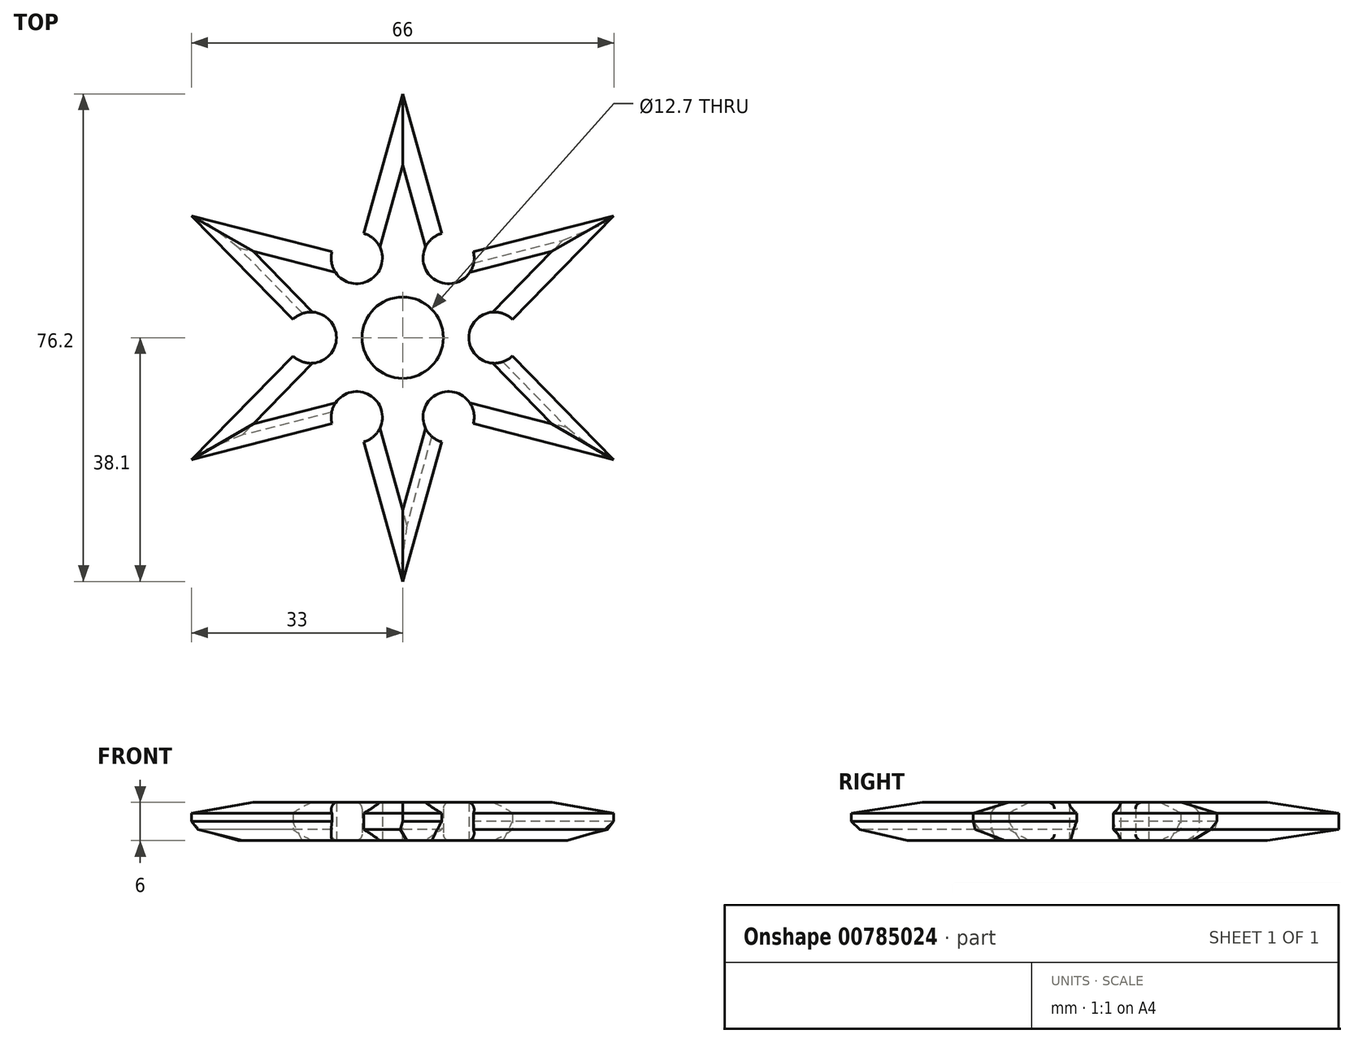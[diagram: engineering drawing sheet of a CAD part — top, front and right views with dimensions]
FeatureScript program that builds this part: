
annotation { "Feature Type Name" : "Feature", "Feature Type Description" : "" }
export const myFeature = defineFeature(function(context is Context, id is Id, definition is map)
    precondition{}
    {
        {
            var Q0;
            Q0=qCreatedBy(makeId("Top.planeOp"),FACE);
            var sketch = newSketch(context, id + "F0", { "sketchPlane" : qUnion([Q0])});
            skCircle(sketch, "E0", {"center": v(0, 0) * mm, "radius": 6.35 * mm});
            skLineSegment(sketch, "E1", {"start": v(0, 38.1) * mm, "end": v(-6.1, 16.28) * mm});
            skLineSegment(sketch, "E2.MirrorCS", {"start": v(0, 38.1) * mm, "end": v(6.1, 16.28) * mm});
            skLineSegment(sketch, "E3.1.0", {"start": v(-33, 19.05) * mm, "end": v(-11.05, 13.42) * mm});
            skLineSegment(sketch, "E3.1.1", {"start": v(-33, 19.05) * mm, "end": v(-17.15, 2.86) * mm});
            skLineSegment(sketch, "E3.2.0", {"start": v(-33, -19.05) * mm, "end": v(-17.15, -2.86) * mm});
            skLineSegment(sketch, "E3.2.1", {"start": v(-33, -19.05) * mm, "end": v(-11.05, -13.42) * mm});
            skLineSegment(sketch, "E3.3.0", {"start": v(0, -38.1) * mm, "end": v(-6.1, -16.28) * mm});
            skLineSegment(sketch, "E3.3.1", {"start": v(0, -38.1) * mm, "end": v(6.1, -16.28) * mm});
            skLineSegment(sketch, "E3.4.0", {"start": v(33, -19.05) * mm, "end": v(11.05, -13.42) * mm});
            skLineSegment(sketch, "E3.4.1", {"start": v(33, -19.05) * mm, "end": v(17.15, -2.86) * mm});
            skLineSegment(sketch, "E3.5.0", {"start": v(33, 19.05) * mm, "end": v(17.15, 2.86) * mm});
            skLineSegment(sketch, "E3.5.1", {"start": v(33, 19.05) * mm, "end": v(11.05, 13.42) * mm});
            skArc(sketch, "E4", {"start": v(-11.05, 13.42) * mm, "mid": v(-5.18, 8.96) * mm, "end": v(-6.1, 16.28) * mm});
            skArc(sketch, "E5.1.0", {"start": v(-17.15, -2.86) * mm, "mid": v(-10.35, 0) * mm, "end": v(-17.15, 2.86) * mm});
            skArc(sketch, "E5.2.0", {"start": v(-6.1, -16.28) * mm, "mid": v(-5.17, -8.96) * mm, "end": v(-11.05, -13.42) * mm});
            skArc(sketch, "E5.3.0", {"start": v(11.05, -13.42) * mm, "mid": v(5.18, -8.96) * mm, "end": v(6.1, -16.28) * mm});
            skArc(sketch, "E5.4.0", {"start": v(17.15, 2.86) * mm, "mid": v(10.35, 0) * mm, "end": v(17.15, -2.86) * mm});
            skArc(sketch, "E5.5.0", {"start": v(6.1, 16.28) * mm, "mid": v(5.17, 8.96) * mm, "end": v(11.05, 13.42) * mm});
            skPoint(sketch, "E6.orphan", {"position": v(7.18, 12.43) * mm});
            skSolve(sketch);
        }
        {
            var Q0;
            Q0=makeQuery(id+"F0.imprint","IMPRINT",FACE,{"disambiguationData":[TD([[makeQuery(id+"F0.imprint","IMPRINT",EDGE,{"derivedFrom":sQuery(id+"F0.wireOp",EDGE,"E0")}),-1.0]])]});
            extrude(context, id + "F1", {"entities" : qUnion([Q0]), "depth" : 6 * mm, "offsetDistance" : 25 * mm});
        }
        {
            var Q0;
            Q0=makeQuery(id+"F1.opExtrude","CAP_EDGE",EDGE,{"disambiguationData":[OSD([sQuery(id+"F0.wireOp",EDGE,"E1")])],"isStart":false});
            var Q1;
            Q1=makeQuery(id+"F1.opExtrude","CAP_EDGE",EDGE,{"disambiguationData":[OSD([sQuery(id+"F0.wireOp",EDGE,"E2.MirrorCS")])],"isStart":false});
            var Q2;
            Q2=makeQuery(id+"F1.opExtrude","CAP_EDGE",EDGE,{"disambiguationData":[OSD([sQuery(id+"F0.wireOp",EDGE,"E3.5.1")])],"isStart":false});
            var Q3;
            Q3=makeQuery(id+"F1.opExtrude","CAP_EDGE",EDGE,{"disambiguationData":[OSD([sQuery(id+"F0.wireOp",EDGE,"E3.5.0")])],"isStart":false});
            var Q4;
            Q4=makeQuery(id+"F1.opExtrude","CAP_EDGE",EDGE,{"disambiguationData":[OSD([sQuery(id+"F0.wireOp",EDGE,"E3.4.1")])],"isStart":false});
            var Q5;
            Q5=makeQuery(id+"F1.opExtrude","CAP_EDGE",EDGE,{"disambiguationData":[OSD([sQuery(id+"F0.wireOp",EDGE,"E3.4.0")])],"isStart":false});
            var Q6;
            Q6=makeQuery(id+"F1.opExtrude","CAP_EDGE",EDGE,{"disambiguationData":[OSD([sQuery(id+"F0.wireOp",EDGE,"E3.3.1")])],"isStart":false});
            var Q7;
            Q7=makeQuery(id+"F1.opExtrude","CAP_EDGE",EDGE,{"disambiguationData":[OSD([sQuery(id+"F0.wireOp",EDGE,"E3.3.0")])],"isStart":false});
            var Q8;
            Q8=makeQuery(id+"F1.opExtrude","CAP_EDGE",EDGE,{"disambiguationData":[OSD([sQuery(id+"F0.wireOp",EDGE,"E3.2.1")])],"isStart":false});
            var Q9;
            Q9=makeQuery(id+"F1.opExtrude","CAP_EDGE",EDGE,{"disambiguationData":[OSD([sQuery(id+"F0.wireOp",EDGE,"E3.2.0")])],"isStart":false});
            var Q10;
            Q10=makeQuery(id+"F1.opExtrude","CAP_EDGE",EDGE,{"disambiguationData":[OSD([sQuery(id+"F0.wireOp",EDGE,"E3.1.1")])],"isStart":false});
            var Q11;
            Q11=makeQuery(id+"F1.opExtrude","CAP_EDGE",EDGE,{"disambiguationData":[OSD([sQuery(id+"F0.wireOp",EDGE,"E3.1.0")])],"isStart":false});
            var Q12;
            Q12=makeQuery(id+"F1.opExtrude","CAP_EDGE",EDGE,{"disambiguationData":[OSD([sQuery(id+"F0.wireOp",EDGE,"E3.3.1")])],"isStart":true});
            var Q13;
            Q13=makeQuery(id+"F1.opExtrude","CAP_EDGE",EDGE,{"disambiguationData":[OSD([sQuery(id+"F0.wireOp",EDGE,"E3.3.0")])],"isStart":true});
            var Q14;
            Q14=makeQuery(id+"F1.opExtrude","CAP_EDGE",EDGE,{"disambiguationData":[OSD([sQuery(id+"F0.wireOp",EDGE,"E3.2.1")])],"isStart":true});
            var Q15;
            Q15=makeQuery(id+"F1.opExtrude","CAP_EDGE",EDGE,{"disambiguationData":[OSD([sQuery(id+"F0.wireOp",EDGE,"E3.2.0")])],"isStart":true});
            var Q16;
            Q16=makeQuery(id+"F1.opExtrude","CAP_EDGE",EDGE,{"disambiguationData":[OSD([sQuery(id+"F0.wireOp",EDGE,"E3.1.1")])],"isStart":true});
            var Q17;
            Q17=makeQuery(id+"F1.opExtrude","CAP_EDGE",EDGE,{"disambiguationData":[OSD([sQuery(id+"F0.wireOp",EDGE,"E3.1.0")])],"isStart":true});
            var Q18;
            Q18=makeQuery(id+"F1.opExtrude","CAP_EDGE",EDGE,{"disambiguationData":[OSD([sQuery(id+"F0.wireOp",EDGE,"E1")])],"isStart":true});
            var Q19;
            Q19=makeQuery(id+"F1.opExtrude","CAP_EDGE",EDGE,{"disambiguationData":[OSD([sQuery(id+"F0.wireOp",EDGE,"E2.MirrorCS")])],"isStart":true});
            var Q20;
            Q20=makeQuery(id+"F1.opExtrude","CAP_EDGE",EDGE,{"disambiguationData":[OSD([sQuery(id+"F0.wireOp",EDGE,"E3.5.1")])],"isStart":true});
            var Q21;
            Q21=makeQuery(id+"F1.opExtrude","CAP_EDGE",EDGE,{"disambiguationData":[OSD([sQuery(id+"F0.wireOp",EDGE,"E3.5.0")])],"isStart":true});
            var Q22;
            Q22=makeQuery(id+"F1.opExtrude","CAP_EDGE",EDGE,{"disambiguationData":[OSD([sQuery(id+"F0.wireOp",EDGE,"E3.4.1")])],"isStart":true});
            var Q23;
            Q23=makeQuery(id+"F1.opExtrude","CAP_EDGE",EDGE,{"disambiguationData":[OSD([sQuery(id+"F0.wireOp",EDGE,"E3.4.0")])],"isStart":true});
            chamfer(context, id + "F2", {"entities" : qUnion([Q0, Q1, Q2, Q3, Q4, Q5, Q6, Q7, Q8, Q9, Q10, Q11, Q12, Q13, Q14, Q15, Q16, Q17, Q18, Q19, Q20, Q21, Q22, Q23]), "chamferType" : ChamferType.OFFSET_ANGLE, "width" : 3 * mm, "oppositeDirection" : false, "angle" : 30 * degree, "tangentPropagation" : true});
        }
        {
            var Q0;
            Q0=makeQuery(id+"F1.opExtrude","CAP_EDGE",EDGE,{"disambiguationData":[OSD([sQuery(id+"F0.wireOp",EDGE,"E0")])],"isStart":true});
            var Q1;
            Q1=makeQuery(id+"F1.opExtrude","CAP_EDGE",EDGE,{"disambiguationData":[OSD([sQuery(id+"F0.wireOp",EDGE,"E0")])],"isStart":false});
            fillet(context, id + "F3", {"entities" : qUnion([Q0, Q1]), "radius" : 1 * mm, "tangentPropagation" : true, "allowEdgeOverflow" : false});
        }
    });
